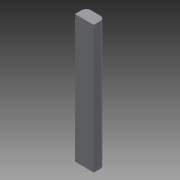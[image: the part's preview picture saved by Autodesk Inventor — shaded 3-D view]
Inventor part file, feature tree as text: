
AUTODESK INVENTOR PART (.ipt)
format: ipt  version: 2013 (Build 170138000, 138)  size: 84,992 bytes
history: native  units: in
note: dims shown in document units (in); Inventor stores cm internally (conversion verified against a paired STEP export)
features: extrude x2, sketch x2, fillet x1
ambient origin geometry x8: Origin, YZ Plane, XZ Plane, XY Plane, X Axis, Y Axis, Z Axis, Center Point
bodies: Solid1 (feature_tree)
feature tree (5):
  extrude  "Extrusion1"  Depth=3.0in
  fillet  "Fillet1"  Radius=5.0in
  extrude  "Extrusion2"  Depth=3.0in TaperAngle=0.0deg
  sketch  "Sketch1"  dims[d0=5.0in d1=3.0in d2=5.0in]
  sketch  "Sketch2"  dims[d3=38.0in d4=3.0in d5=0.0in d6=1.25in d7=4.0in d8=0.0in]
